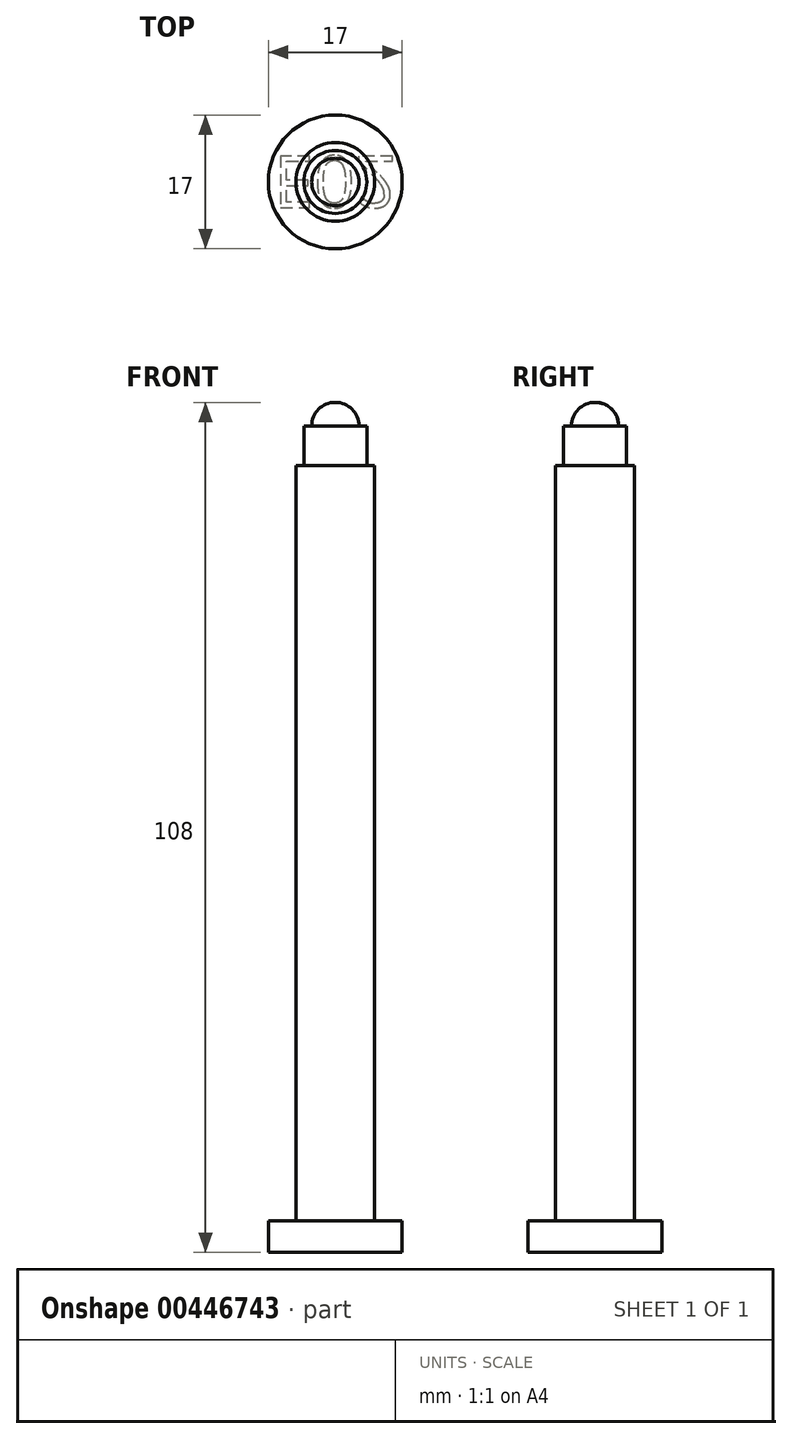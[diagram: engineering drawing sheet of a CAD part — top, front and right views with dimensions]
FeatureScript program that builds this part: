
annotation { "Feature Type Name" : "Feature", "Feature Type Description" : "" }
export const myFeature = defineFeature(function(context is Context, id is Id, definition is map)
    precondition{}
    {
        {
            var Q0;
            Q0=qCreatedBy(makeId("Top.planeOp"),FACE);
            var sketch = newSketch(context, id + "F0", { "sketchPlane" : qUnion([Q0])});
            skCircle(sketch, "E0", {"center": v(0, 0) * mm, "radius": 8.5 * mm});
            skSolve(sketch);
        }
        {
            var Q0;
            Q0=qSketchRegion(id+"F0",true);
            extrude(context, id + "F1", {"entities" : qUnion([Q0]), "depth" : 4 * mm});
        }
        {
            var Q0;
            Q0=qCreatedBy(makeId("Top.planeOp"),FACE);
            var sketch = newSketch(context, id + "F2", { "sketchPlane" : qUnion([Q0])});
            skCircle(sketch, "E1", {"center": v(0, 0) * mm, "radius": 5 * mm});
            skSolve(sketch);
        }
        {
            var Q0;
            Q0=qSketchRegion(id+"F2",true);
            extrude(context, id + "F3", {"entities" : qUnion([Q0]), "operationType" : NewBodyOperationType.ADD, "depth" : 100 * mm});
        }
        {
            var Q0;
            Q0=qCreatedBy(makeId("Right.planeOp"),FACE);
            var sketch = newSketch(context, id + "F4", { "sketchPlane" : qUnion([Q0])});
            skLineSegment(sketch, "E2", {"start": v(0, 105) * mm, "end": v(0, 100) * mm});
            skLineSegment(sketch, "E3", {"start": v(0, 100) * mm, "end": v(4, 100) * mm});
            skLineSegment(sketch, "E4", {"start": v(4, 100) * mm, "end": v(4, 105) * mm});
            skLineSegment(sketch, "E5", {"start": v(4, 105) * mm, "end": v(0, 105) * mm});
            skSolve(sketch);
        }
        {
            var Q0;
            Q0=makeQuery(id+"F4.imprint","IMPRINT",FACE,{"disambiguationData":[TD([[makeQuery(id+"F4.imprint","IMPRINT",EDGE,{"derivedFrom":sQuery(id+"F4.wireOp",EDGE,"E2")}),1.0]])]});
            var Q1;
            Q1=sQuery(id+"F4.wireOp",EDGE,"E2");
            revolve(context, id + "F5", {"operationType" : NewBodyOperationType.ADD, "entities" : qUnion([Q0]), "axis" : qUnion([Q1]), "revolveType" : RevolveType.FULL});
        }
        {
            var Q0;
            Q0=qCreatedBy(makeId("Right.planeOp"),FACE);
            var sketch = newSketch(context, id + "F6", { "sketchPlane" : qUnion([Q0])});
            skLineSegment(sketch, "E6", {"start": v(0, 108) * mm, "end": v(0, 105) * mm});
            skLineSegment(sketch, "E7", {"start": v(0, 105) * mm, "end": v(3, 105) * mm});
            skArc(sketch, "E8", {"start": v(3, 105) * mm, "mid": v(2.12, 107.12) * mm, "end": v(0, 108) * mm});
            skSolve(sketch);
        }
        {
            var Q0;
            Q0=makeQuery(id+"F6.imprint","IMPRINT",FACE,{"disambiguationData":[TD([[makeQuery(id+"F6.imprint","IMPRINT",EDGE,{"derivedFrom":sQuery(id+"F6.wireOp",EDGE,"E6")}),1.0]])]});
            var Q1;
            Q1=sQuery(id+"F6.wireOp",EDGE,"E6");
            revolve(context, id + "F7", {"operationType" : NewBodyOperationType.ADD, "entities" : qUnion([Q0]), "axis" : qUnion([Q1]), "revolveType" : RevolveType.FULL});
        }
        {
            var Q0;
            Q0=makeQuery(id+"F1.opExtrude","CAP_FACE",FACE,{"disambiguationData":[OSD([sQuery(id+"F0.wireOp",EDGE,"E0")])],"isStart":true});
            var sketch = newSketch(context, id + "F8", { "sketchPlane" : qUnion([Q0])});
            skText(sketch, "E9", { "text": "E02\n", "fontName": "OpenSans-Regular.ttf"});
            const initialGuessF8  = {"E9": [-0.00783, -0.0033, 1, 0, 0.0066]};
            skSetInitialGuess(sketch, initialGuessF8);
            skSolve(sketch);
        }
        {
            var Q0;
            Q0=qSketchRegion(id+"F8",true);
            extrude(context, id + "F9", {"entities" : qUnion([Q0]), "operationType" : NewBodyOperationType.REMOVE, "oppositeDirection" : true, "depth" : 0.1 * mm, "offsetDistance" : 25 * mm});
        }
    });
